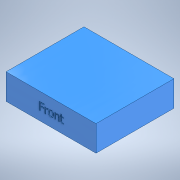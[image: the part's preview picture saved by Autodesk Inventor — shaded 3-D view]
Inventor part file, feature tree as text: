
AUTODESK INVENTOR PART (.ipt)
format: ipt  version: 2022.2 (Build 262287000, 287)  size: 324,608 bytes
history: native  units: mm
features: sketch x3, extrude x2, emboss x2
ambient origin geometry x8: Origin, YZ Plane, XZ Plane, XY Plane, X Axis, Y Axis, Z Axis, Center Point
bodies: Body1 (feature_tree)
feature tree (7):
  sketch  "Sketch33"  dims[d95=15.0mm d178=118.7mm]
  extrude  "Extrusion26"  Depth=118.7mm
  extrude  "Extrusion27"  Depth=10.0mm
  sketch  "Sketch34"  dims[d179=137.0mm d180=10.0mm]
  sketch  "Sketch35"  dims[d181=10.0mm d182=8.0mm d183=0.0mm d184=31.0mm d185=0.0mm d186=1.0mm d187=0.0mm d188=1.0mm d189=0.0mm]
  emboss  "Emboss1"
  emboss  "Emboss2"
